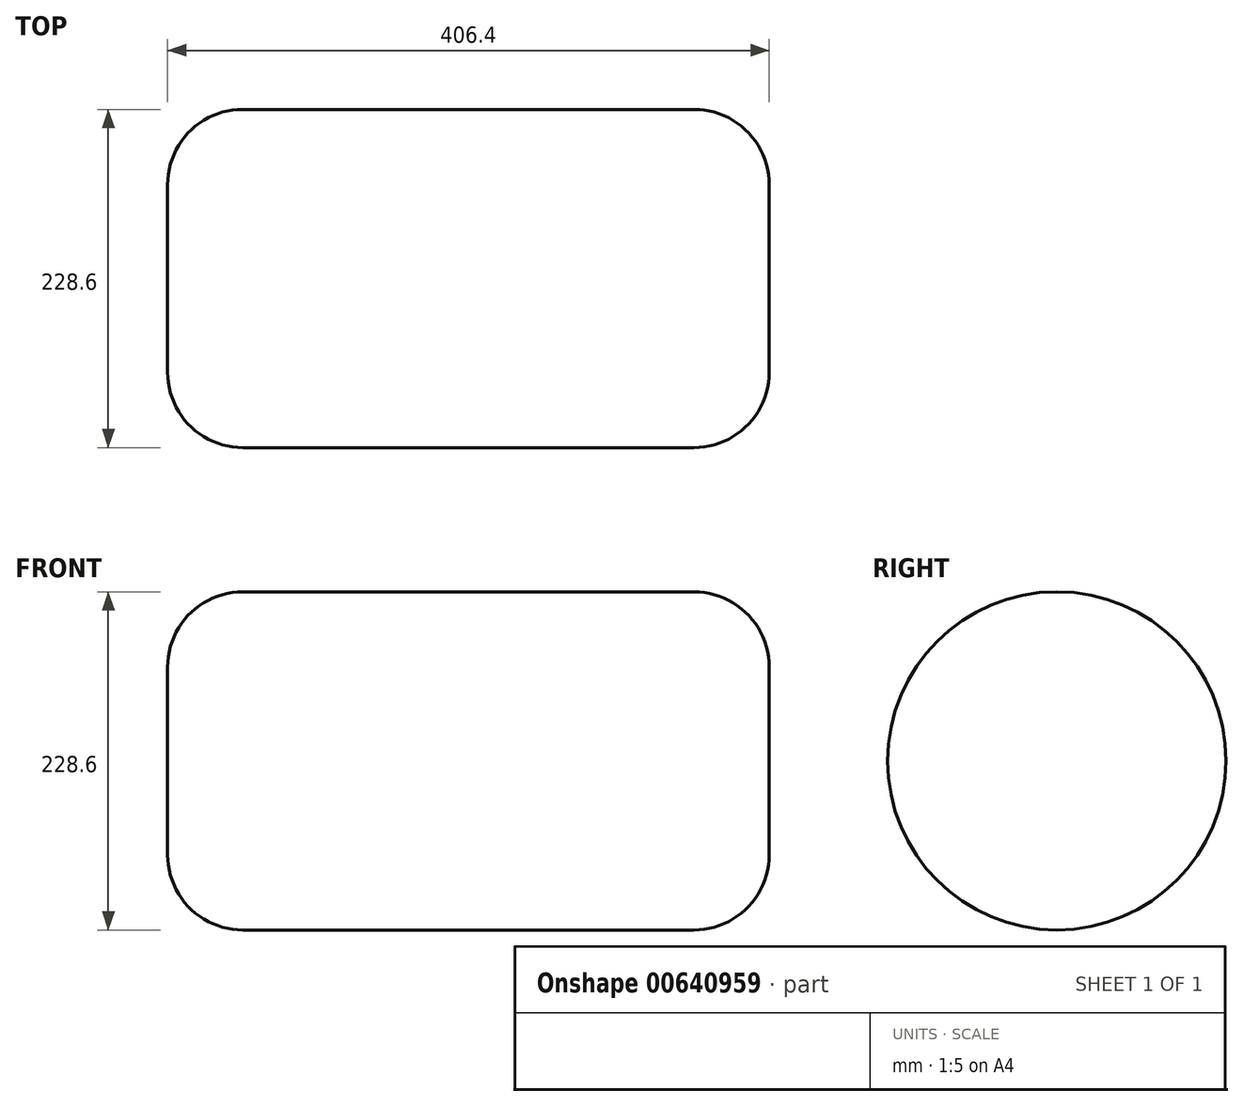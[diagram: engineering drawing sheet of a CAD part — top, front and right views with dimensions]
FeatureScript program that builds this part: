
annotation { "Feature Type Name" : "Feature", "Feature Type Description" : "" }
export const myFeature = defineFeature(function(context is Context, id is Id, definition is map)
    precondition{}
    {
        {
            var Q0;
            Q0=qCreatedBy(makeId("Right.planeOp"),FACE);
            var sketch = newSketch(context, id + "F0", { "sketchPlane" : qUnion([Q0])});
            skCircle(sketch, "E0", {"center": v(0, 0) * mm, "radius": 114.3 * mm});
            skSolve(sketch);
        }
        {
            var Q0;
            Q0=qSketchRegion(id+"F0",true);
            extrude(context, id + "F1", {"entities" : qUnion([Q0]), "depth" : 406.4 * mm, "offsetDistance" : 25.4 * mm});
        }
        {
            var Q0;
            Q0=makeQuery(id+"F1.opExtrude","CAP_EDGE",EDGE,{"disambiguationData":[OSD([sQuery(id+"F0.wireOp",EDGE,"E0")])],"isStart":true});
            var Q1;
            Q1=makeQuery(id+"F1.opExtrude","CAP_EDGE",EDGE,{"disambiguationData":[OSD([sQuery(id+"F0.wireOp",EDGE,"E0")])],"isStart":false});
            fillet(context, id + "F2", {"entities" : qUnion([Q0, Q1]), "radius" : 50.8 * mm, "tangentPropagation" : true, "allowEdgeOverflow" : false});
        }
    });
